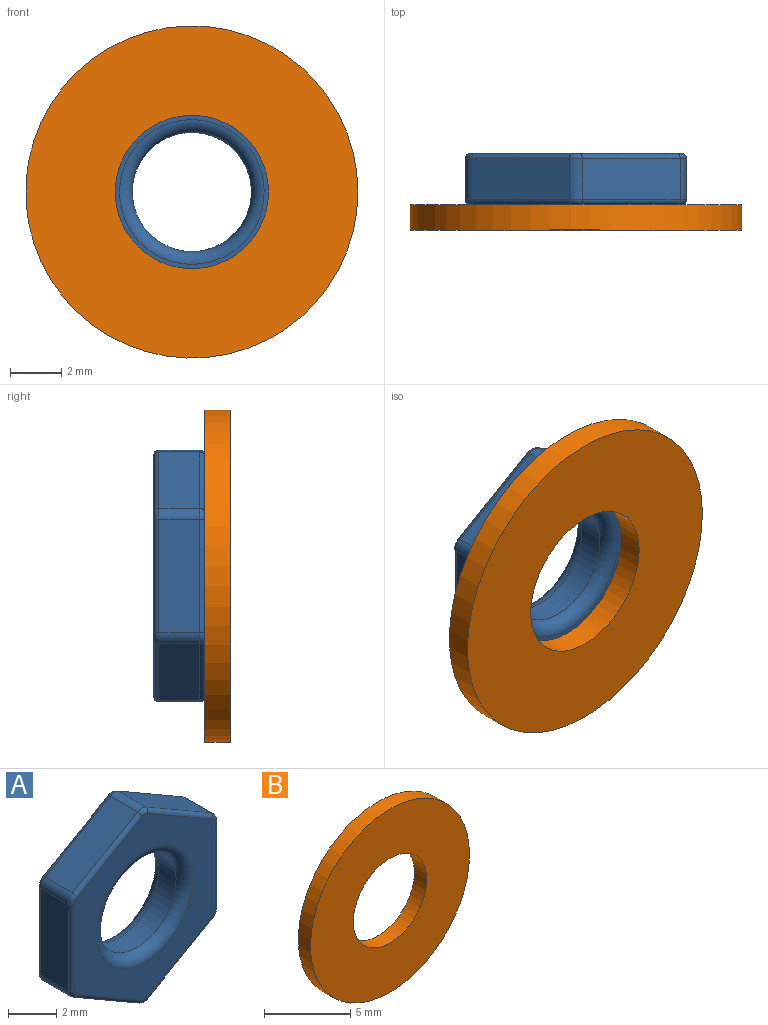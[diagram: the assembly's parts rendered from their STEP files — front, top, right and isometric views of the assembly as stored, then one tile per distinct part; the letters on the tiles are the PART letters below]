
ASSEMBLY  parts=2 mates=1
PART A: 41 faces, bbox 8.7x2x9.9 mm
  f0: plane 3.83x2.21mm, normal (-0.5,0,-0.87), area 7.1mm2, adj f11,f16,f23,f31
  f1: plane 3.83x2.21mm, normal (0.5,0,-0.87), area 7.1mm2, adj f11,f12,f19,f35
  f2: plane 4.42x1.6mm, normal (1,0,0), area 7.1mm2, adj f12,f13,f18,f39
  f3: plane 3.83x2.21mm, normal (0.5,0,0.87), area 7.1mm2, adj f13,f14,f22,f38
  f4: plane 3.83x2.21mm, normal (-0.5,0,0.87), area 7.1mm2, adj f14,f15,f26,f34
  f5: plane 4.42x1.6mm, normal (-1,0,0), area 7.1mm2, adj f15,f16,f27,f30
  f6: plane 9.45x8.26mm, normal (0,-1,0), area 33.9mm2, adj f10,f17,f18,f19,f20,f21,f22,f23
  f7: plane 9.45x8.26mm, normal (0,1,0), area 33.9mm2, adj f9,f29,f30,f31,f32,f33,f34,f35
  f8: cylinder r=2.33mm len=4.66mm, axis (0,-1,0), area 14.6mm2, adj f9,f10
  f9: torus R=2.83mm, axis (0,-1,0), area 12.4mm2, adj f7,f8
  f10: torus R=2.83mm, axis (0,-1,0), area 12.4mm2, adj f6,f8
  f11: cylinder r=0.5mm len=1.6mm, axis (0,1,0), area 0.8mm2, adj f0,f1,f21,f33
  f12: cylinder r=0.5mm len=1.6mm, axis (0,1,0), area 0.8mm2, adj f1,f2,f17,f37
  f13: cylinder r=0.5mm len=1.6mm, axis (0,1,0), area 0.8mm2, adj f2,f3,f20,f40
  f14: cylinder r=0.5mm len=1.6mm, axis (0,1,0), area 0.8mm2, adj f3,f4,f24,f36
  f15: cylinder r=0.5mm len=1.6mm, axis (0,1,0), area 0.8mm2, adj f4,f5,f28,f32
  f16: cylinder r=0.5mm len=1.6mm, axis (0,1,0), area 0.8mm2, adj f0,f5,f25,f29
  f17: torus R=0.3mm, axis (0,-1,0), area 0.1mm2, adj f6,f12,f18,f19
  f18: cylinder r=0.2mm len=4.42mm, axis (0,0,-1), area 1.4mm2, adj f2,f6,f17,f20
  f19: cylinder r=0.2mm len=3.93mm, axis (-0.87,0,-0.5), area 1.4mm2, adj f1,f6,f17,f21
  f20: torus R=0.3mm, axis (0,-1,0), area 0.1mm2, adj f6,f13,f18,f22
  f21: torus R=0.3mm, axis (0,-1,0), area 0.1mm2, adj f6,f11,f19,f23
  f22: cylinder r=0.2mm len=3.93mm, axis (0.87,0,-0.5), area 1.4mm2, adj f3,f6,f20,f24
  f23: cylinder r=0.2mm len=3.93mm, axis (-0.87,0,0.5), area 1.4mm2, adj f0,f6,f21,f25
  f24: torus R=0.3mm, axis (0,-1,0), area 0.1mm2, adj f6,f14,f22,f26
  f25: torus R=0.3mm, axis (0,-1,0), area 0.1mm2, adj f6,f16,f23,f27
  f26: cylinder r=0.2mm len=3.93mm, axis (0.87,0,0.5), area 1.4mm2, adj f4,f6,f24,f28
  f27: cylinder r=0.2mm len=4.42mm, axis (0,0,1), area 1.4mm2, adj f5,f6,f25,f28
  f28: torus R=0.3mm, axis (0,-1,0), area 0.1mm2, adj f6,f15,f26,f27
  f29: torus R=0.3mm, axis (0,-1,0), area 0.1mm2, adj f7,f16,f30,f31
  f30: cylinder r=0.2mm len=4.42mm, axis (0,0,-1), area 1.4mm2, adj f5,f7,f29,f32
  f31: cylinder r=0.2mm len=3.93mm, axis (0.87,0,-0.5), area 1.4mm2, adj f0,f7,f29,f33
  f32: torus R=0.3mm, axis (0,-1,0), area 0.1mm2, adj f7,f15,f30,f34
  f33: torus R=0.3mm, axis (0,-1,0), area 0.1mm2, adj f7,f11,f31,f35
  f34: cylinder r=0.2mm len=3.93mm, axis (-0.87,0,-0.5), area 1.4mm2, adj f4,f7,f32,f36
  f35: cylinder r=0.2mm len=3.93mm, axis (0.87,0,0.5), area 1.4mm2, adj f1,f7,f33,f37
  f36: torus R=0.3mm, axis (0,-1,0), area 0.1mm2, adj f7,f14,f34,f38
  f37: torus R=0.3mm, axis (0,-1,0), area 0.1mm2, adj f7,f12,f35,f39
  f38: cylinder r=0.2mm len=3.93mm, axis (-0.87,0,0.5), area 1.4mm2, adj f3,f7,f36,f40
  f39: cylinder r=0.2mm len=4.42mm, axis (0,0,1), area 1.4mm2, adj f2,f7,f37,f40
  f40: torus R=0.3mm, axis (0,-1,0), area 0.1mm2, adj f7,f13,f38,f39
PART B: 4 faces, bbox 13x1x13 mm
  f0: cylinder r=3mm len=6mm, axis (0,1,0), area 18.8mm2, adj f2,f3
  f1: cylinder r=6.5mm len=13mm, axis (0,1,0), area 40.8mm2, adj f2,f3
  f2: plane 13x13mm, normal (0,-1,0), area 104.5mm2, adj f0,f1
  f3: plane 13x13mm, normal (0,1,0), area 104.5mm2, adj f0,f1
PLACE A t=(0,1.5,0)mm
PLACE B at identity
MATE fastened B.f0 <-> A.f8  axis (0,1,0) through (0,0.5,0)mm
